AUTODESK INVENTOR PART (.ipt)
format: ipt  version: 2017 (Build 210142000, 142)  size: 190,976 bytes
history: native  units: mm
features: other x18, extrude x8, sketch x7, projected_geometry x3, plane x2, revolve x1, pattern_circular x1, mirror x1, chamfer x1, fillet x1, pattern_linear x1
ambient origin geometry x8: Origin, YZ Plane, XZ Plane, XY Plane, X Axis, Y Axis, Z Axis, Center Point
bodies: Solid1 (feature_tree)
feature tree (44):
  other  "Table"
  other  "Part Number = Promag L400 DN25"
  other  "Part Number = Promag L400 DN32"
  other  "Part Number = Promag L400 DN40"
  other  "Part Number = Promag L400 DN50"
  other  "Part Number = Promag L400 DN65"
  other  "Part Number = Promag L400 DN80"
  other  "Part Number = Promag L400 DN100"
  other  "Part Number = Promag L400 DN125"
  other  "Part Number = Promag L400 DN150"
  other  "Part Number = Promag L400 DN200"
  other  "Part Number = Promag L400 DN250"
  other  "Part Number = Promag L400 DN300"
  other  "Part Number = Promag L400 DN350"
  other  "Part Number = Promag L400 DN400"
  other  "Part Number = Promag L400 DN450"
  other  "Part Number = Promag L400 DN500"
  other  "Part Number = Promag L400 DN600"
  revolve  "Revolution1"  Angle=90.0deg
  extrude  "Extrusion1"  Depth=10.0mm TaperAngle=0.0deg
  pattern_circular  "Circular Pattern1"  Count=9  [1 undecoded]
  mirror  "Mirror1"
  extrude  "Extrusion2"  Depth=103.0mm
  chamfer  "Chamfer1"  Distance=167.0mm
  extrude  "Extrusion3"  Depth=85.0mm TaperAngle=0.0deg
  extrude  "Extrusion4"  Depth=900.0mm
  extrude  "Extrusion6"  Depth=1.0mm
  extrude  "Extrusion5"  Depth=90.0mm TaperAngle=0.0deg
  plane  "Work Plane2"
  extrude  "Extrusion9"  Depth=8.0mm TaperAngle=0.0deg
  plane  "Work Plane1"
  extrude  "Extrusion8"  [1 undecoded]
  fillet  "Fillet2"  Radius=25.0mm
  pattern_linear  "Rectangular Pattern2"  Spacing1=25.0mm  [1 undecoded]
  sketch  "Sketch2"  dims[d3=45.0deg d10=90.0deg]
  sketch  "Sketch3"  dims[d13=45.0deg d14=10.0mm d15=0.0mm]
  sketch  "Sketch4"  dims[d17=360.0deg]
  sketch  "Sketch5"  dims[d24=0.0mm]
  sketch  "Sketch6"  dims[d25=47.0mm d26=2.0mm d27=45.0deg]
  sketch  "Sketch7"  dims[d28=94.0mm]
  projected_geometry  "Projected Loop1"
  projected_geometry  "Projected Loop3"
  sketch  "Sketch11"  dims[d29=138.0mm d30=0.0mm d31=90.0mm d32=103.0mm d33=167.0mm d34=85.0mm d35=0.0mm d36=900.0mm d38=1.0mm d39=90.0mm d40=0.0mm d45=8.0mm d46=0.0mm d47=-20.0mm d51=25.0mm d52=25.0mm d53=0.0mm d54=5.0mm d58=-20.0mm d60=2.0mm d61=0.0mm d62=30.0mm d64=50.0mm d65=0.0mm d72=20.0mm d73=20.0mm d74=20.0mm d75=60.0mm d76=3.0mm]
  projected_geometry  "Projected Loop4"
note: 3 required parameter values undecoded (feature->parameter linkage not recoverable at this tier; creation-order binding heuristic only, values carry confidence <= 0.55)
